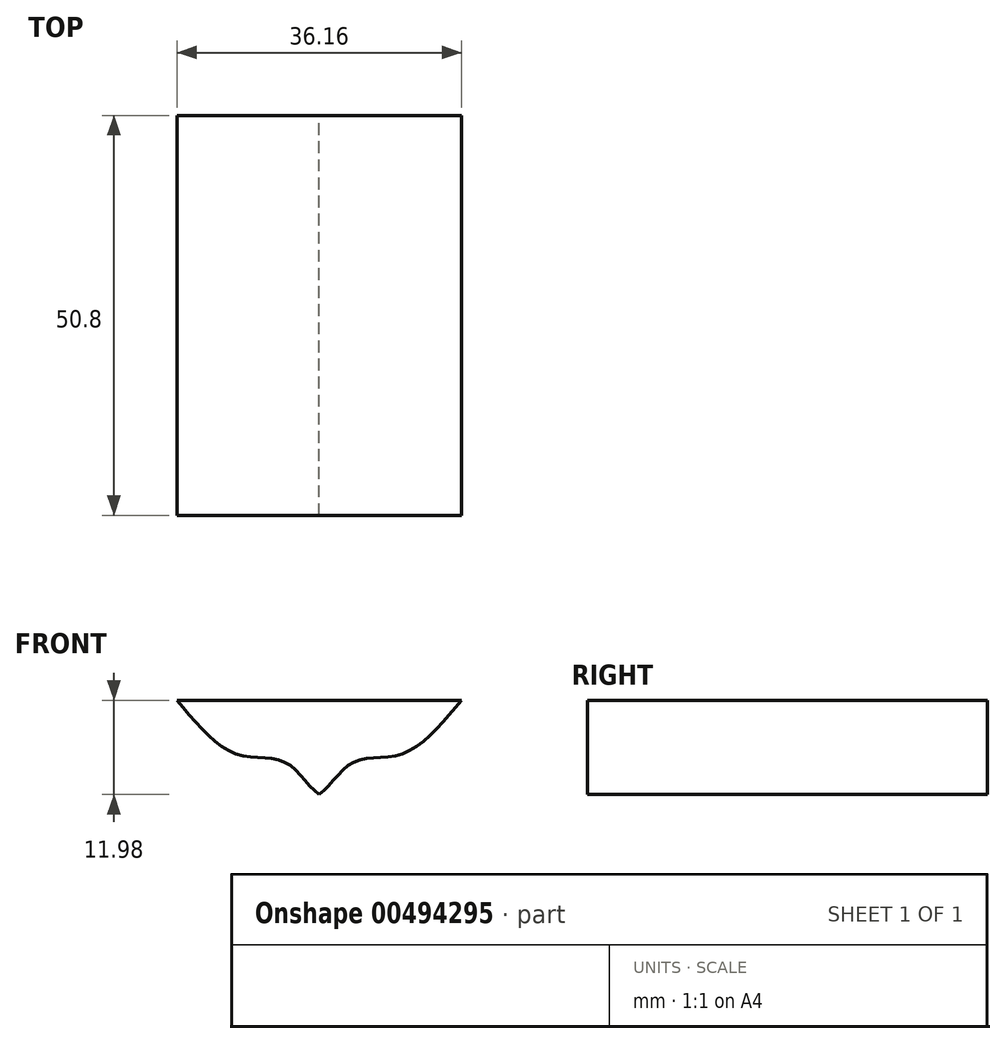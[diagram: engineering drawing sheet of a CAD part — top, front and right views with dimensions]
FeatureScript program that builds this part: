
annotation { "Feature Type Name" : "Feature", "Feature Type Description" : "" }
export const myFeature = defineFeature(function(context is Context, id is Id, definition is map)
    precondition{}
    {
        {
            var Q0;
            Q0=qCreatedBy(makeId("Front.planeOp"),FACE);
            var sketch = newSketch(context, id + "F0", { "sketchPlane" : qUnion([Q0])});
            skFitSpline(sketch, "E0", {"points": [v(-28.48, 17.86) * mm, v(-21.02, 11.07) * mm, v(-14.7, 9.94) * mm, v(-10.4, 5.88) * mm], "startDerivative": vector(17.9, -21.22) * mm, "endDerivative": vector(14.3, -9.99) * mm});
            skLineSegment(sketch, "E1", {"start": v(-10.4, 19.77) * mm, "end": v(-10.4, 0) * mm});
            skLineSegment(sketch, "E2", {"start": v(-28.48, 17.86) * mm, "end": v(-10.4, 17.86) * mm});
            skFitSpline(sketch, "E3.MirrorCS", {"points": [v(7.68, 17.86) * mm, v(0.23, 11.07) * mm, v(-6.1, 9.94) * mm, v(-10.4, 5.88) * mm], "startDerivative": vector(-17.9, -21.22) * mm, "endDerivative": vector(-14.3, -9.99) * mm});
            skLineSegment(sketch, "E4.MirrorCS", {"start": v(7.68, 17.86) * mm, "end": v(-10.4, 17.86) * mm});
            skSolve(sketch);
        }
        {
            var Q0;
            {var subQ0=sQuery(id+"F0.wireOp",EDGE,"E0");Q0=makeQuery(id+"F0.imprint","IMPRINT",FACE,{"disambiguationData":[TD([[makeQuery(id+"F0.imprint","IMPRINT",EDGE,{"derivedFrom":subQ0}),1.0]])]});}
            var Q1;
            {var subQ0=sQuery(id+"F0.wireOp",EDGE,"E3.MirrorCS");Q1=makeQuery(id+"F0.imprint","IMPRINT",FACE,{"disambiguationData":[TD([[makeQuery(id+"F0.imprint","IMPRINT",EDGE,{"derivedFrom":subQ0}),-1.0]])]});}
            extrude(context, id + "F1", {"entities" : qUnion([Q0, Q1]), "depth" : 25.4 * mm, "hasSecondDirection" : true, "secondDirectionOppositeDirection" : true, "secondDirectionDepth" : 25.4 * mm});
        }
    });
